# Revit family: 2025.3.19
name_source: partatom
category: Doors
units: mm (PartAtom-declared; Revit-internal decimal feet)

## family parameters
Always vertical = Yes
Cut with Voids When Loaded = No
Host = Wall
Room Calculation Point = No
Shared = No

## types (20) — shared parameters
Default Elevation = 0' - 0"
Height = 14' - 0"
Height above ground = 4' - 0"
Height of Door = 14' - 0"
Width of Switch = 1' - 0"
depth of Switch = 0' - 5"
height of Switch = 1' - 4"

## per-type parameters (varying)
| type | LAYOUT A | LAYOUT B | LAYOUT C | LAYOUT D | LAYOUT E | LAYOUT F | LAYOUT G | LAYOUT H | LAYOUT J | LAYOUT K | Width | Width of Door |
| LAYOUT A 14'x14' | Yes | No | No | No | No | No | No | No | No | No | 14' - 0" | 14' - 0" |
| LAYOUT B 14'x14' | No | Yes | No | No | No | No | No | No | No | No | 14' - 0" | 14' - 0" |
| LAYOUT C 14'x14' | No | No | Yes | No | No | No | No | No | No | No | 14' - 0" | 14' - 0" |
| LAYOUT D 14'x14' | No | No | No | Yes | No | No | No | No | No | No | 14' - 0" | 14' - 0" |
| LAYOUT E 14'x14' | No | No | No | No | Yes | No | No | No | No | No | 14' - 0" | 14' - 0" |
| LAYOUT F 14'x14' | No | No | No | No | No | Yes | No | No | No | No | 14' - 0" | 14' - 0" |
| LAYOUT A 12'x14' | Yes | No | No | No | No | No | No | No | No | No | 12' - 0" | 12' - 0" |
| LAYOUT B 12'x14' | No | Yes | No | No | No | No | No | No | No | No | 12' - 0" | 12' - 0" |
| LAYOUT C 12'x14' | No | No | Yes | No | No | No | No | No | No | No | 12' - 0" | 12' - 0" |
| LAYOUT D 12'x14' | No | No | No | Yes | No | No | No | No | No | No | 12' - 0" | 12' - 0" |
| LAYOUT E 12'x14' | No | No | No | No | Yes | No | No | No | No | No | 12' - 0" | 12' - 0" |
| LAYOUT F 12'x14' | No | No | No | No | No | Yes | No | No | No | No | 12' - 0" | 12' - 0" |
| LAYOUT G 12'x14' | No | No | No | No | No | No | Yes | No | No | No | 12' - 0" | 12' - 0" |
| LAYOUT G 14'x14' | No | No | No | No | No | No | Yes | No | No | No | 14' - 0" | 14' - 0" |
| LAYOUT H 12'x14' | No | No | No | No | No | No | No | Yes | No | No | 12' - 0" | 12' - 0" |
| LAYOUT H 14'x14' | No | No | No | No | No | No | No | Yes | No | No | 14' - 0" | 14' - 0" |
| LAYOUT J 12'x14' | No | No | No | No | No | No | No | No | Yes | No | 12' - 0" | 12' - 0" |
| LAYOUT J 14'x14' | No | No | No | No | No | No | No | No | Yes | No | 14' - 0" | 14' - 0" |
| LAYOUT K 12'x14' | No | No | No | No | No | No | No | No | No | Yes | 12' - 0" | 12' - 0" |
| LAYOUT K 14'x14' | No | No | No | No | No | No | No | No | No | Yes | 14' - 0" | 14' - 0" |

## geometry (parser evidence)
native form markers: Sweep x111
no freeform markers — native parametric forms only
